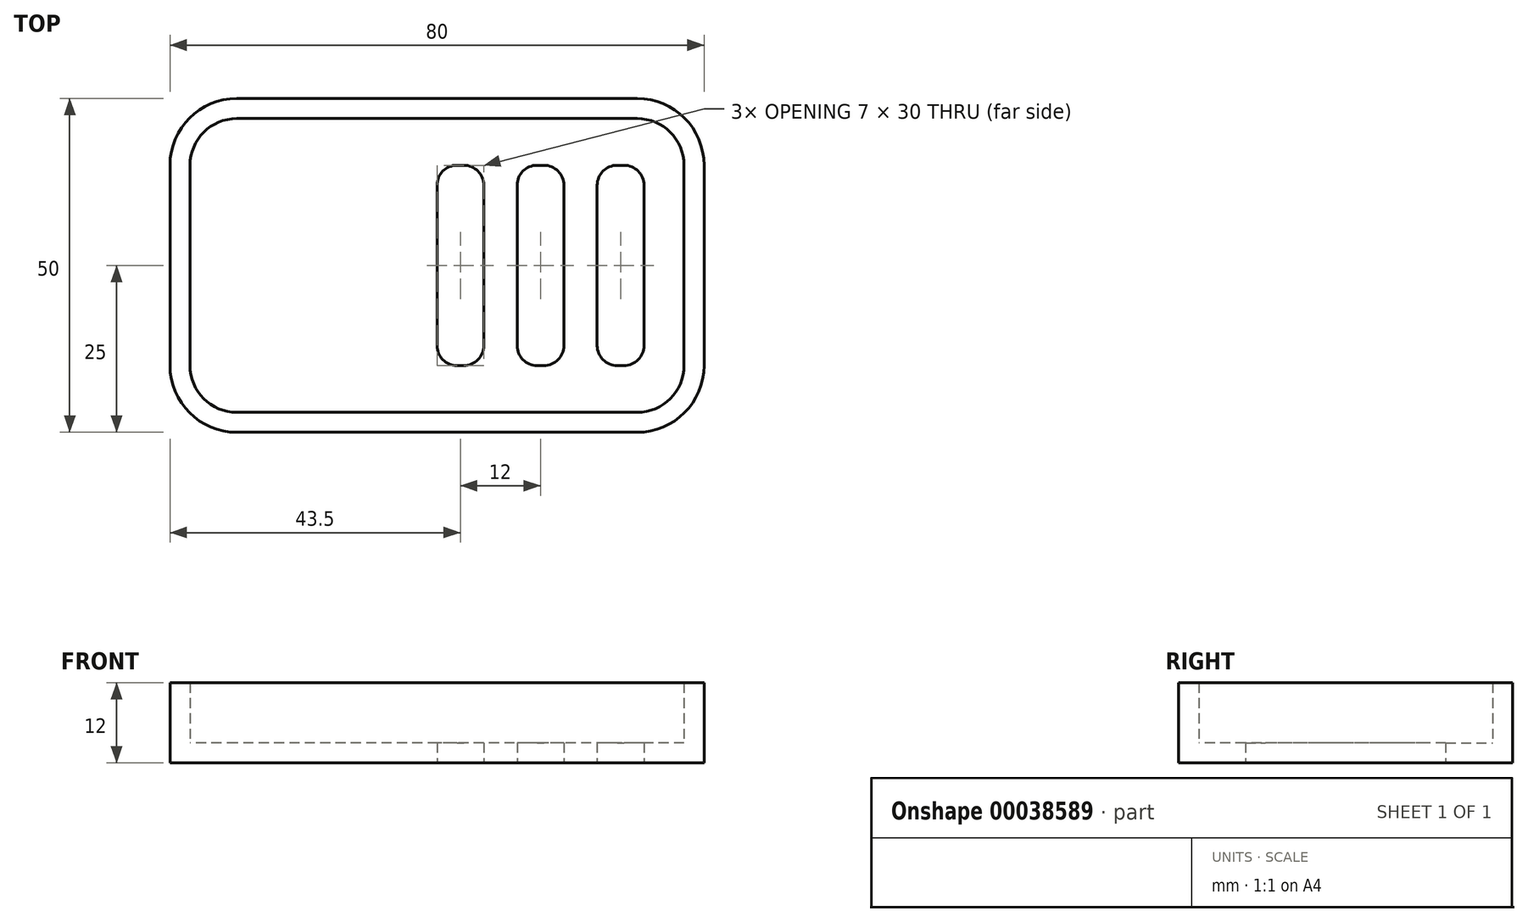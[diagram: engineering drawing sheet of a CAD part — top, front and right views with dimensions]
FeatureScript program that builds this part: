
annotation { "Feature Type Name" : "Feature", "Feature Type Description" : "" }
export const myFeature = defineFeature(function(context is Context, id is Id, definition is map)
    precondition{}
    {
        {
            var Q0;
            Q0=qCreatedBy(makeId("Top.planeOp"),FACE);
            var sketch = newSketch(context, id + "F0", { "sketchPlane" : qUnion([Q0])});
            skLineSegment(sketch, "E0.bottom", {"start": v(30, 25) * mm, "end": v(-30, 25) * mm});
            skLineSegment(sketch, "E0.top", {"start": v(30, -25) * mm, "end": v(-30, -25) * mm});
            skLineSegment(sketch, "E0.left", {"start": v(40, 15) * mm, "end": v(40, -15) * mm});
            skLineSegment(sketch, "E0.right", {"start": v(-40, 15) * mm, "end": v(-40, -15) * mm});
            skPoint(sketch, "E0.middle", {"position": v(0, 0) * mm});
            skPoint(sketch, "E1.visualSharp", {"position": v(-40, 25) * mm});
            skArc(sketch, "E1.filletArc", {"start": v(-30, 25) * mm, "mid": v(-37.07, 22.07) * mm, "end": v(-40, 15) * mm});
            skPoint(sketch, "E2.visualSharp", {"position": v(40, 25) * mm});
            skArc(sketch, "E2.filletArc", {"start": v(40, 15) * mm, "mid": v(37.07, 22.07) * mm, "end": v(30, 25) * mm});
            skPoint(sketch, "E3.visualSharp", {"position": v(40, -25) * mm});
            skArc(sketch, "E3.filletArc", {"start": v(30, -25) * mm, "mid": v(37.07, -22.07) * mm, "end": v(40, -15) * mm});
            skPoint(sketch, "E4.visualSharp", {"position": v(-40, -25) * mm});
            skArc(sketch, "E4.filletArc", {"start": v(-40, -15) * mm, "mid": v(-37.07, -22.07) * mm, "end": v(-30, -25) * mm});
            skArc(sketch, "E5.0", {"start": v(37, 15) * mm, "mid": v(34.95, 19.95) * mm, "end": v(30, 22) * mm});
            skLineSegment(sketch, "E5.1", {"start": v(37, 15) * mm, "end": v(37, -15) * mm});
            skLineSegment(sketch, "E5.2", {"start": v(30, 22) * mm, "end": v(-30, 22) * mm});
            skArc(sketch, "E5.3", {"start": v(30, -22) * mm, "mid": v(34.95, -19.95) * mm, "end": v(37, -15) * mm});
            skArc(sketch, "E5.4", {"start": v(-30, 22) * mm, "mid": v(-34.95, 19.95) * mm, "end": v(-37, 15) * mm});
            skLineSegment(sketch, "E5.5", {"start": v(-37, 15) * mm, "end": v(-37, -15) * mm});
            skArc(sketch, "E5.6", {"start": v(-37, -15) * mm, "mid": v(-34.95, -19.95) * mm, "end": v(-30, -22) * mm});
            skLineSegment(sketch, "E5.7", {"start": v(30, -22) * mm, "end": v(-30, -22) * mm});
            skLineSegment(sketch, "E6.bottom", {"start": v(3, 15) * mm, "end": v(4, 15) * mm});
            skLineSegment(sketch, "E6.top", {"start": v(3, -15) * mm, "end": v(4, -15) * mm});
            skLineSegment(sketch, "E6.left", {"start": v(0, 12) * mm, "end": v(0, -12) * mm});
            skLineSegment(sketch, "E6.right", {"start": v(7, 12) * mm, "end": v(7, -12) * mm});
            skLineSegment(sketch, "E7.direction1", {"start": v(3, -15) * mm, "end": v(4, -15) * mm, "construction": true});
            skPoint(sketch, "E8.visualSharp", {"position": v(0, 15) * mm});
            skArc(sketch, "E8.filletArc", {"start": v(3, 15) * mm, "mid": v(0.88, 14.12) * mm, "end": v(0, 12) * mm});
            skPoint(sketch, "E9.visualSharp", {"position": v(7, 15) * mm});
            skArc(sketch, "E9.filletArc", {"start": v(7, 12) * mm, "mid": v(6.12, 14.12) * mm, "end": v(4, 15) * mm});
            skArc(sketch, "E10.filletArc", {"start": v(0, -12) * mm, "mid": v(0.88, -14.12) * mm, "end": v(3, -15) * mm});
            skArc(sketch, "E11.filletArc", {"start": v(4, -15) * mm, "mid": v(6.12, -14.12) * mm, "end": v(7, -12) * mm});
            skLineSegment(sketch, "E12.1.0.0", {"start": v(19, 12) * mm, "end": v(19, -12) * mm});
            skLineSegment(sketch, "E12.1.0.1", {"start": v(12, 12) * mm, "end": v(12, -12) * mm});
            skPoint(sketch, "E12.1.0.2", {"position": v(12, 15) * mm});
            skArc(sketch, "E12.1.0.3", {"start": v(15, 15) * mm, "mid": v(12.88, 14.12) * mm, "end": v(12, 12) * mm});
            skArc(sketch, "E12.1.0.4", {"start": v(16, -15) * mm, "mid": v(18.12, -14.12) * mm, "end": v(19, -12) * mm});
            skPoint(sketch, "E12.1.0.5", {"position": v(19, 15) * mm});
            skPoint(sketch, "E12.1.0.6", {"position": v(12, 0) * mm});
            skArc(sketch, "E12.1.0.7", {"start": v(12, -12) * mm, "mid": v(12.88, -14.12) * mm, "end": v(15, -15) * mm});
            skArc(sketch, "E12.1.0.8", {"start": v(19, 12) * mm, "mid": v(18.12, 14.12) * mm, "end": v(16, 15) * mm});
            skLineSegment(sketch, "E12.1.0.9", {"start": v(15, 15) * mm, "end": v(16, 15) * mm});
            skLineSegment(sketch, "E12.1.0.10", {"start": v(15, -15) * mm, "end": v(16, -15) * mm, "construction": true});
            skLineSegment(sketch, "E12.1.0.11", {"start": v(15, -15) * mm, "end": v(16, -15) * mm});
            skLineSegment(sketch, "E12.2.0.0", {"start": v(31, 12) * mm, "end": v(31, -12) * mm});
            skLineSegment(sketch, "E12.2.0.1", {"start": v(24, 12) * mm, "end": v(24, -12) * mm});
            skPoint(sketch, "E12.2.0.2", {"position": v(24, 15) * mm});
            skArc(sketch, "E12.2.0.3", {"start": v(27, 15) * mm, "mid": v(24.88, 14.12) * mm, "end": v(24, 12) * mm});
            skArc(sketch, "E12.2.0.4", {"start": v(28, -15) * mm, "mid": v(30.12, -14.12) * mm, "end": v(31, -12) * mm});
            skPoint(sketch, "E12.2.0.5", {"position": v(31, 15) * mm});
            skPoint(sketch, "E12.2.0.6", {"position": v(24, 0) * mm});
            skArc(sketch, "E12.2.0.7", {"start": v(24, -12) * mm, "mid": v(24.88, -14.12) * mm, "end": v(27, -15) * mm});
            skArc(sketch, "E12.2.0.8", {"start": v(31, 12) * mm, "mid": v(30.12, 14.12) * mm, "end": v(28, 15) * mm});
            skLineSegment(sketch, "E12.2.0.9", {"start": v(27, 15) * mm, "end": v(28, 15) * mm});
            skLineSegment(sketch, "E12.2.0.10", {"start": v(27, -15) * mm, "end": v(28, -15) * mm, "construction": true});
            skLineSegment(sketch, "E12.2.0.11", {"start": v(27, -15) * mm, "end": v(28, -15) * mm});
            skLineSegment(sketch, "E12.direction1", {"start": v(3, -15) * mm, "end": v(15, -15) * mm, "construction": true});
            skSolve(sketch);
        }
        {
            var Q0;
            Q0=makeQuery(id+"F0.imprint","IMPRINT",FACE,{"disambiguationData":[TD([[makeQuery(id+"F0.imprint","IMPRINT",EDGE,{"derivedFrom":sQuery(id+"F0.wireOp",EDGE,"E5.0")}),1.0]])]});
            extrude(context, id + "F1", {"entities" : qUnion([Q0]), "depth" : 3 * mm});
        }
        {
            var Q0;
            Q0=makeQuery(id+"F0.imprint","IMPRINT",FACE,{"disambiguationData":[TD([[makeQuery(id+"F0.imprint","IMPRINT",EDGE,{"derivedFrom":sQuery(id+"F0.wireOp",EDGE,"E0.bottom")}),1.0]])]});
            extrude(context, id + "F2", {"entities" : qUnion([Q0]), "operationType" : NewBodyOperationType.ADD, "depth" : 12 * mm});
        }
    });
